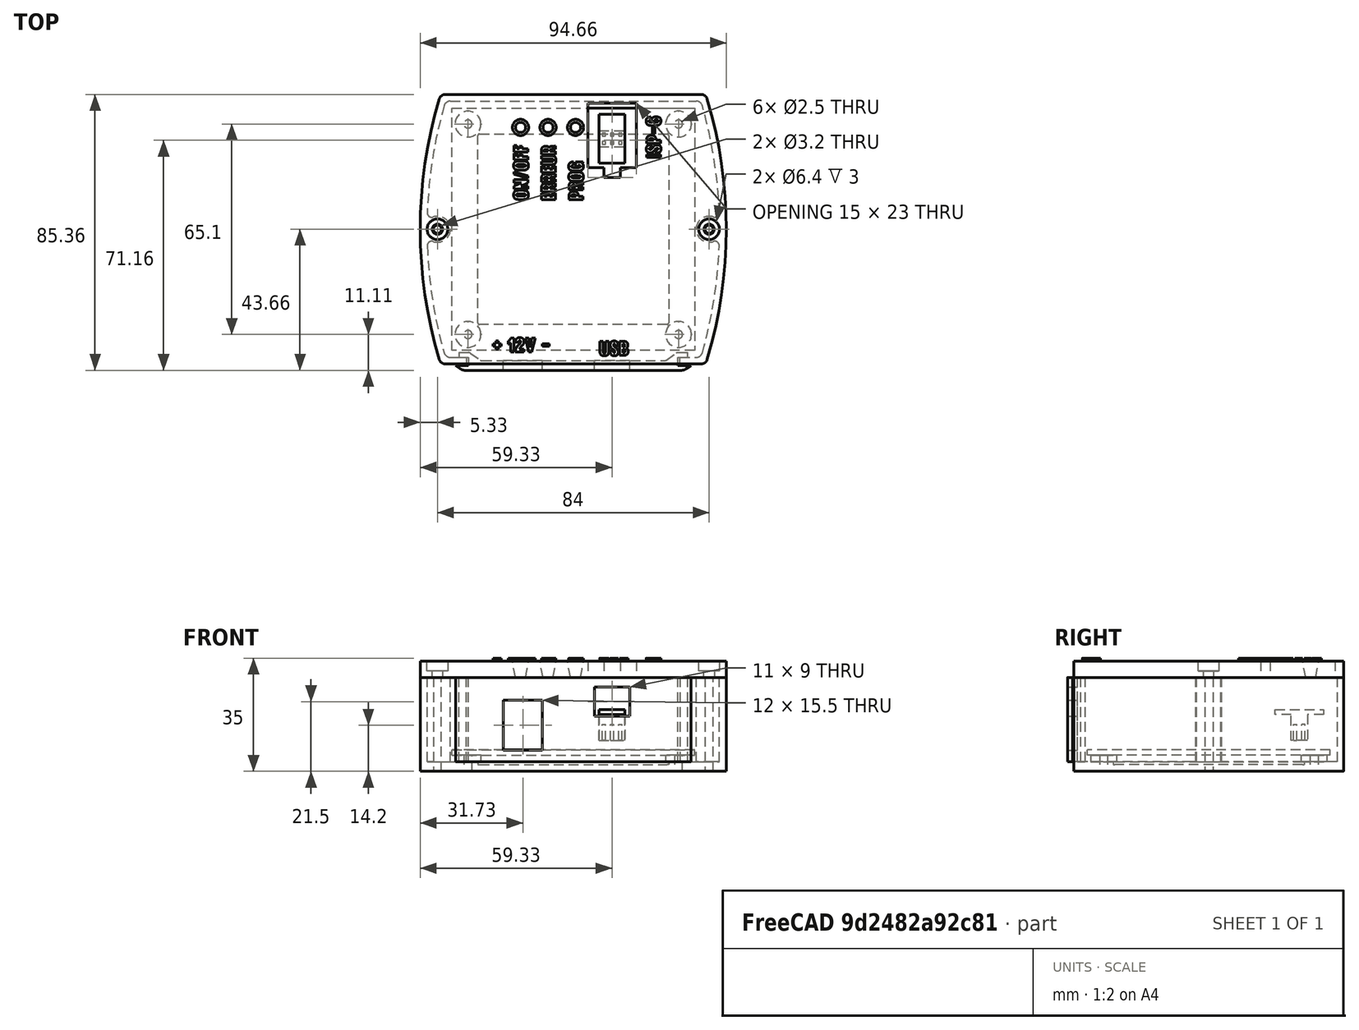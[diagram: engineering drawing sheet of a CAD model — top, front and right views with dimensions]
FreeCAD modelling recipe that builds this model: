
FCSTD DOCUMENT  (FreeCAD 0.16R6706 (Git))
Label: Assemblage
License: All rights reserved
LicenseURL: http://en.wikipedia.org/wiki/All_rights_reserved
objects: Part::Feature×4, Sketcher::SketchObject×1, PartDesign::Pad×1, App::DocumentObjectGroup×1
note: 7 computed .brp shape members not serialized (recipe doc carries the construction recipe); baked Part::Feature solids carry a one-line shape summary decoded from their .brp

FEATURE [Part::Feature] Part__Feature  label="Box-001.step"
  shape: bbox 94.66 x 83.39 x 29 mm, 53 faces (baked)
FEATURE [Part::Feature] Part__Feature001  label="Box-002.step"
  Placement = pos=(0,0,3) rot=(0,0,1;0rad)
  shape: bbox 72.8 x 5.5 x 26 mm, 32 faces (baked)
FEATURE [Part::Feature] Part__Feature002  label="Box-003.step"
  shape: bbox 94.66 x 83.39 x 6 mm, 354 faces (baked)
FEATURE [Sketcher::SketchObject] Sketch  label="Carte"
  Placement = pos=(0,0,5) rot=(0,0,1;0rad)
  sketch-geometry (14):
    g0: LineSegment StartX=-37.5 StartY=37.5 StartZ=0 EndX=37.5 EndY=37.5 EndZ=0
    g1: LineSegment StartX=37.5 StartY=37.5 StartZ=0 EndX=37.5 EndY=-37.5 EndZ=0
    g2: LineSegment StartX=37.5 StartY=-37.5 StartZ=0 EndX=-37.5 EndY=-37.5 EndZ=0
    g3: LineSegment StartX=-37.5 StartY=-37.5 StartZ=0 EndX=-37.5 EndY=37.5 EndZ=0
    g4: Circle [constr] CenterX=0 CenterY=0 CenterZ=0 NormalX=0 NormalY=0 NormalZ=1 Radius=53.033
    g5: Circle [constr] CenterX=-32.5 CenterY=32.5 CenterZ=0 NormalX=0 NormalY=0 NormalZ=1 Radius=3.2
    g6: Circle [constr] CenterX=32.5 CenterY=32.5 CenterZ=0 NormalX=0 NormalY=0 NormalZ=1 Radius=3.2
    g7: Circle [constr] CenterX=32.5 CenterY=-32.5 CenterZ=0 NormalX=0 NormalY=0 NormalZ=1 Radius=3.2
    g8: Circle [constr] CenterX=-32.5 CenterY=-32.5 CenterZ=0 NormalX=0 NormalY=0 NormalZ=1 Radius=3.2
    g9: Circle [constr] CenterX=0 CenterY=0 CenterZ=0 NormalX=0 NormalY=0 NormalZ=1 Radius=45.9619
    g10: LineSegment [constr] StartX=-32.5 StartY=32.5 StartZ=0 EndX=32.5 EndY=32.5 EndZ=0
    g11: LineSegment [constr] StartX=32.5 StartY=32.5 StartZ=0 EndX=32.5 EndY=-32.5 EndZ=0
    g12: LineSegment [constr] StartX=32.5 StartY=-32.5 StartZ=0 EndX=-32.5 EndY=-32.5 EndZ=0
    g13: LineSegment [constr] StartX=-32.5 StartY=-32.5 StartZ=0 EndX=-32.5 EndY=32.5 EndZ=0
  constraints (36):
    c: Coincident(g0,g1)
    c: Coincident(g1,g2)
    c: Coincident(g2,g3)
    c: Coincident(g3,g0)
    c: Horizontal(g0)
    c: Horizontal(g2)
    c: Vertical(g1)
    c: Vertical(g3)
    c: DistanceX(g0,g0) = 75
    c: DistanceY(g1,g1) = 75
    c: Coincident(g4,g-1)
    c: PointOnObject(g0,g4)
    c: PointOnObject(g0,g4)
    c: PointOnObject(g1,g4)
    c: Radius(g5) = 3.2
    c: Equal(g5,g6)
    c: Equal(g5,g7)
    c: Equal(g5,g8)
    c: Coincident(g9,g-1)
    c: Coincident(g10,g11)
    c: Coincident(g11,g12)
    c: Coincident(g12,g13)
    c: Coincident(g13,g10)
    c: Horizontal(g10)
    c: Horizontal(g12)
    c: Vertical(g11)
    c: Vertical(g13)
    c: PointOnObject(g10,g9)
    c: PointOnObject(g11,g9)
    c: Equal(g10,g11)
    c: DistanceX(g10,g10) = 65
    c: PointOnObject(g10,g9)
    c: Coincident(g8,g12)
    c: Coincident(g7,g11)
    c: Coincident(g5,g10)
    c: Coincident(g6,g10)
FEATURE [PartDesign::Pad] Pad
  Length = 1.6
  Length2 = 100
  Placement = pos=(0,0,5) rot=(0,0,1;0rad)
  Sketch = -> Sketch
  Type = 0
FEATURE [App::DocumentObjectGroup] Groupe  label="Carte001"
  Group = -> [Pad]
FEATURE [Part::Feature] Part__Feature003  label="Prise-ISP-6.step"
  Placement = pos=(12,28,17.5) rot=(0,0,1;0rad)
  shape: bbox 8 x 15 x 9.6 mm, 42 faces (baked)
